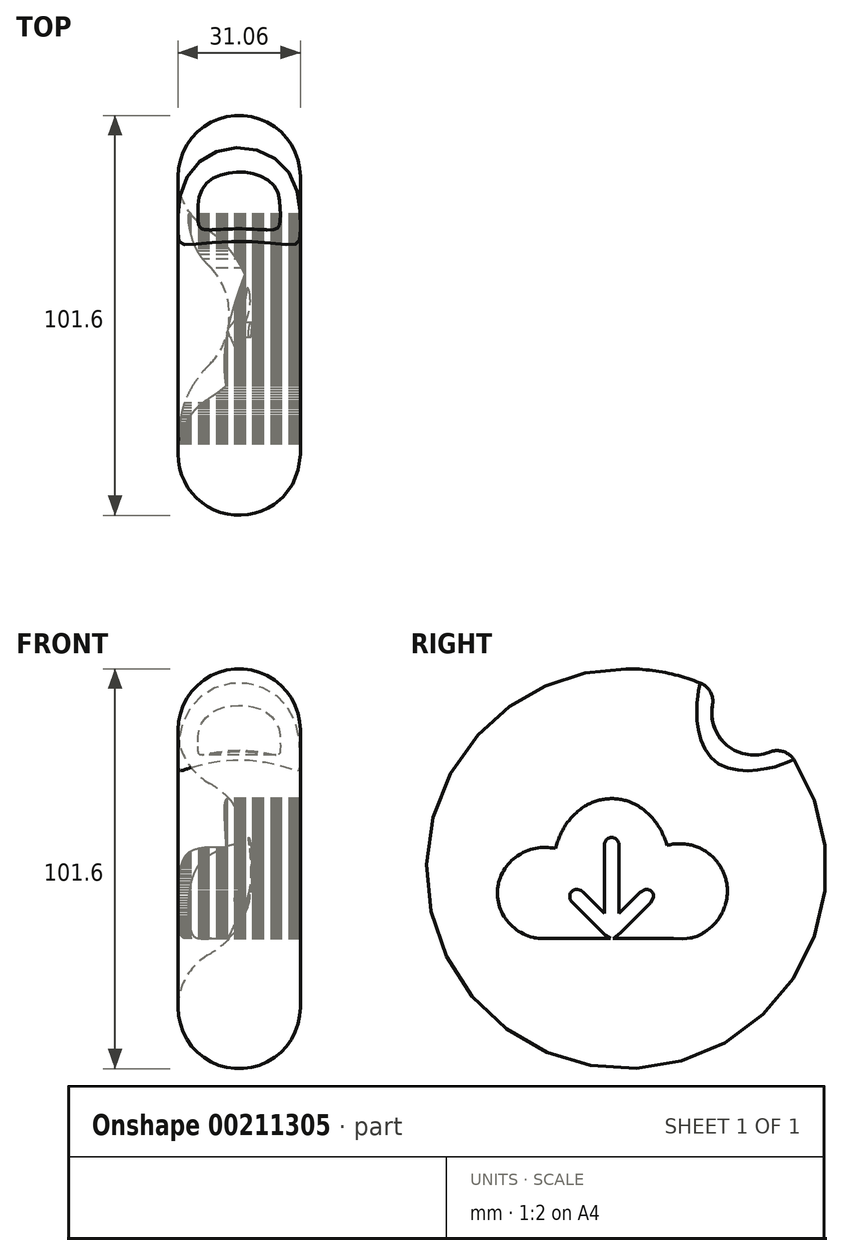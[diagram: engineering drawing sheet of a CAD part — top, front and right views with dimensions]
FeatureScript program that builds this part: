
annotation { "Feature Type Name" : "Feature", "Feature Type Description" : "" }
export const myFeature = defineFeature(function(context is Context, id is Id, definition is map)
    precondition{}
    {
        {
            var Q0;
            Q0=qCreatedBy(makeId("Top.planeOp"),FACE);
            var sketch = newSketch(context, id + "F0", { "sketchPlane" : qUnion([Q0])});
            skArc(sketch, "E0", {"start": v(10.16, -18.2) * mm, "mid": v(18.8, -9) * mm, "end": v(20.56, 3.5) * mm});
            skArc(sketch, "E1", {"start": v(10.16, -18.2) * mm, "mid": v(9.87, -45.16) * mm, "end": v(33.26, -31.77) * mm});
            skLineSegment(sketch, "E2", {"start": v(33.26, -4.3) * mm, "end": v(33.26, 3.5) * mm});
            skLineSegment(sketch, "E3", {"start": v(33.26, -4.3) * mm, "end": v(33.26, -31.77) * mm});
            skLineSegment(sketch, "E4", {"start": v(20.56, 3.5) * mm, "end": v(46.67, 3.5) * mm});
            skPoint(sketch, "E5.orphan", {"position": v(33.26, 20.85) * mm});
            skSolve(sketch);
        }
        {
            var Q0;
            {var subQ1=sQuery(id+"F0.wireOp",EDGE,"E0");Q0=makeQuery(id+"F0.imprint","IMPRINT",FACE,{"disambiguationData":[TD([[makeQuery(id+"F0.imprint","IMPRINT",EDGE,{"derivedFrom":subQ1}),-1.0]])]});}
            var Q1;
            Q1=sQuery(id+"F0.wireOp",EDGE,"E4");
            revolve(context, id + "F1", {"entities" : qUnion([Q0]), "axis" : qUnion([Q1]), "revolveType" : RevolveType.FULL});
        }
        {
            var Q0;
            Q0=qCreatedBy(makeId("Right.planeOp"),FACE);
            var sketch = newSketch(context, id + "F2", { "sketchPlane" : qUnion([Q0])});
            skCircle(sketch, "E6", {"center": v(35.9, 39.54) * mm, "radius": 10.68 * mm});
            skSolve(sketch);
        }
        {
            var Q0;
            Q0=makeQuery(id+"F2.imprint","IMPRINT",FACE,{"disambiguationData":[TD([[makeQuery(id+"F2.imprint","IMPRINT",EDGE,{"derivedFrom":sQuery(id+"F2.wireOp",EDGE,"E6")}),1.0]])]});
            extrude(context, id + "F3", {"entities" : qUnion([Q0]), "operationType" : NewBodyOperationType.REMOVE, "depth" : 53.85 * mm});
        }
        {
            var Q0;
            Q0=makeQuery(id+"F3.boolean.opBoolean","INTERSECT",EDGE,{"derivedFrom":[makeQuery(id+"F1.opRevolve","SWEPT_FACE",FACE,{"disambiguationData":[OSD([sQuery(id+"F0.wireOp",EDGE,"E1")])]}),makeQuery(id+"F3.opExtrude","SWEPT_FACE",FACE,{"disambiguationData":[OSD([sQuery(id+"F2.wireOp",EDGE,"E6")])]})]});
            fillet(context, id + "F4", {"entities" : qUnion([Q0]), "radius" : 5.08 * mm, "tangentPropagation" : true, "allowEdgeOverflow" : false});
        }
        {
            var Q0;
            Q0=qCreatedBy(makeId("Right.planeOp"),FACE);
            var sketch = newSketch(context, id + "F5", { "sketchPlane" : qUnion([Q0])});
            skLineSegment(sketch, "E7", {"start": v(-6.98, 15.9) * mm, "end": v(-6.63, 16.1) * mm});
            skLineSegment(sketch, "E8", {"start": v(-6.63, 16.1) * mm, "end": v(-6.28, 16.3) * mm});
            skLineSegment(sketch, "E9", {"start": v(-6.28, 16.3) * mm, "end": v(-5.92, 16.48) * mm});
            skLineSegment(sketch, "E10", {"start": v(-5.92, 16.48) * mm, "end": v(-5.56, 16.65) * mm});
            skLineSegment(sketch, "E11", {"start": v(-5.56, 16.65) * mm, "end": v(-5.2, 16.8) * mm});
            skLineSegment(sketch, "E12", {"start": v(-5.2, 16.8) * mm, "end": v(-4.82, 16.95) * mm});
            skLineSegment(sketch, "E13", {"start": v(-4.82, 16.95) * mm, "end": v(-4.45, 17.09) * mm});
            skLineSegment(sketch, "E14", {"start": v(-4.45, 17.09) * mm, "end": v(-4.07, 17.21) * mm});
            skLineSegment(sketch, "E15", {"start": v(-4.07, 17.21) * mm, "end": v(-3.68, 17.32) * mm});
            skLineSegment(sketch, "E16", {"start": v(-3.68, 17.32) * mm, "end": v(-3.3, 17.43) * mm});
            skLineSegment(sketch, "E17", {"start": v(-3.3, 17.43) * mm, "end": v(-2.9, 17.51) * mm});
            skLineSegment(sketch, "E18", {"start": v(-2.9, 17.51) * mm, "end": v(-2.51, 17.6) * mm});
            skLineSegment(sketch, "E19", {"start": v(-2.51, 17.6) * mm, "end": v(-2.12, 17.66) * mm});
            skLineSegment(sketch, "E20", {"start": v(-2.12, 17.66) * mm, "end": v(-1.72, 17.71) * mm});
            skLineSegment(sketch, "E21", {"start": v(-1.72, 17.71) * mm, "end": v(-1.32, 17.75) * mm});
            skLineSegment(sketch, "E22", {"start": v(-1.32, 17.75) * mm, "end": v(-0.92, 17.78) * mm});
            skLineSegment(sketch, "E23", {"start": v(-0.92, 17.78) * mm, "end": v(-0.52, 17.8) * mm});
            skLineSegment(sketch, "E24", {"start": v(-0.52, 17.8) * mm, "end": v(-0.12, 17.8) * mm});
            skLineSegment(sketch, "E25", {"start": v(-0.12, 17.8) * mm, "end": v(0.28, 17.8) * mm});
            skLineSegment(sketch, "E26", {"start": v(0.28, 17.8) * mm, "end": v(0.68, 17.78) * mm});
            skLineSegment(sketch, "E27", {"start": v(0.68, 17.78) * mm, "end": v(1.08, 17.75) * mm});
            skLineSegment(sketch, "E28", {"start": v(1.08, 17.75) * mm, "end": v(1.47, 17.7) * mm});
            skLineSegment(sketch, "E29", {"start": v(1.47, 17.7) * mm, "end": v(1.87, 17.65) * mm});
            skLineSegment(sketch, "E30", {"start": v(1.87, 17.65) * mm, "end": v(2.26, 17.58) * mm});
            skLineSegment(sketch, "E31", {"start": v(2.26, 17.58) * mm, "end": v(2.66, 17.5) * mm});
            skLineSegment(sketch, "E32", {"start": v(2.66, 17.5) * mm, "end": v(3.05, 17.4) * mm});
            skLineSegment(sketch, "E33", {"start": v(3.05, 17.4) * mm, "end": v(3.43, 17.3) * mm});
            skLineSegment(sketch, "E34", {"start": v(3.43, 17.3) * mm, "end": v(3.82, 17.18) * mm});
            skLineSegment(sketch, "E35", {"start": v(3.82, 17.18) * mm, "end": v(4.2, 17.05) * mm});
            skLineSegment(sketch, "E36", {"start": v(4.2, 17.05) * mm, "end": v(4.7, 16.86) * mm});
            skLineSegment(sketch, "E37", {"start": v(4.7, 16.86) * mm, "end": v(5.18, 16.65) * mm});
            skLineSegment(sketch, "E38", {"start": v(5.18, 16.65) * mm, "end": v(5.66, 16.42) * mm});
            skLineSegment(sketch, "E39", {"start": v(5.66, 16.42) * mm, "end": v(6.13, 16.17) * mm});
            skLineSegment(sketch, "E40", {"start": v(6.13, 16.17) * mm, "end": v(6.58, 15.91) * mm});
            skLineSegment(sketch, "E41", {"start": v(6.58, 15.91) * mm, "end": v(7.03, 15.63) * mm});
            skLineSegment(sketch, "E42", {"start": v(7.03, 15.63) * mm, "end": v(7.46, 15.34) * mm});
            skLineSegment(sketch, "E43", {"start": v(7.46, 15.34) * mm, "end": v(7.88, 15.02) * mm});
            skLineSegment(sketch, "E44", {"start": v(7.88, 15.02) * mm, "end": v(8.3, 14.7) * mm});
            skLineSegment(sketch, "E45", {"start": v(8.3, 14.7) * mm, "end": v(8.7, 14.36) * mm});
            skLineSegment(sketch, "E46", {"start": v(8.7, 14.36) * mm, "end": v(9.08, 14) * mm});
            skLineSegment(sketch, "E47", {"start": v(9.08, 14) * mm, "end": v(9.46, 13.63) * mm});
            skLineSegment(sketch, "E48", {"start": v(9.46, 13.63) * mm, "end": v(9.82, 13.25) * mm});
            skLineSegment(sketch, "E49", {"start": v(9.82, 13.25) * mm, "end": v(10.17, 12.86) * mm});
            skLineSegment(sketch, "E50", {"start": v(10.17, 12.86) * mm, "end": v(10.51, 12.45) * mm});
            skLineSegment(sketch, "E51", {"start": v(10.51, 12.45) * mm, "end": v(10.84, 12.04) * mm});
            skLineSegment(sketch, "E52", {"start": v(10.84, 12.04) * mm, "end": v(11.15, 11.61) * mm});
            skLineSegment(sketch, "E53", {"start": v(11.15, 11.61) * mm, "end": v(11.46, 11.18) * mm});
            skLineSegment(sketch, "E54", {"start": v(11.46, 11.18) * mm, "end": v(11.74, 10.73) * mm});
            skLineSegment(sketch, "E55", {"start": v(11.74, 10.73) * mm, "end": v(12.02, 10.28) * mm});
            skLineSegment(sketch, "E56", {"start": v(12.02, 10.28) * mm, "end": v(12.28, 9.82) * mm});
            skLineSegment(sketch, "E57", {"start": v(12.28, 9.82) * mm, "end": v(12.53, 9.35) * mm});
            skLineSegment(sketch, "E58", {"start": v(12.53, 9.35) * mm, "end": v(12.76, 8.88) * mm});
            skLineSegment(sketch, "E59", {"start": v(12.76, 8.88) * mm, "end": v(12.98, 8.4) * mm});
            skLineSegment(sketch, "E60", {"start": v(12.98, 8.4) * mm, "end": v(13.19, 7.9) * mm});
            skLineSegment(sketch, "E61", {"start": v(13.19, 7.9) * mm, "end": v(13.38, 7.42) * mm});
            skLineSegment(sketch, "E62", {"start": v(13.38, 7.42) * mm, "end": v(13.56, 6.92) * mm});
            skLineSegment(sketch, "E63", {"start": v(13.56, 6.92) * mm, "end": v(13.72, 6.42) * mm});
            skLineSegment(sketch, "E64", {"start": v(13.72, 6.42) * mm, "end": v(13.87, 5.92) * mm});
            skLineSegment(sketch, "E65", {"start": v(13.87, 5.92) * mm, "end": v(14.25, 6.02) * mm});
            skLineSegment(sketch, "E66", {"start": v(14.25, 6.02) * mm, "end": v(14.63, 6.1) * mm});
            skLineSegment(sketch, "E67", {"start": v(14.63, 6.1) * mm, "end": v(15, 6.18) * mm});
            skLineSegment(sketch, "E68", {"start": v(15, 6.18) * mm, "end": v(15.4, 6.24) * mm});
            skLineSegment(sketch, "E69", {"start": v(15.4, 6.24) * mm, "end": v(15.78, 6.3) * mm});
            skLineSegment(sketch, "E70", {"start": v(15.78, 6.3) * mm, "end": v(16.17, 6.33) * mm});
            skLineSegment(sketch, "E71", {"start": v(16.17, 6.33) * mm, "end": v(16.56, 6.35) * mm});
            skLineSegment(sketch, "E72", {"start": v(16.56, 6.35) * mm, "end": v(16.94, 6.36) * mm});
            skLineSegment(sketch, "E73", {"start": v(16.94, 6.36) * mm, "end": v(17.33, 6.36) * mm});
            skLineSegment(sketch, "E74", {"start": v(17.33, 6.36) * mm, "end": v(17.72, 6.35) * mm});
            skLineSegment(sketch, "E75", {"start": v(17.72, 6.35) * mm, "end": v(18.11, 6.32) * mm});
            skLineSegment(sketch, "E76", {"start": v(18.11, 6.32) * mm, "end": v(18.5, 6.28) * mm});
            skLineSegment(sketch, "E77", {"start": v(18.5, 6.28) * mm, "end": v(18.88, 6.23) * mm});
            skLineSegment(sketch, "E78", {"start": v(18.88, 6.23) * mm, "end": v(19.27, 6.17) * mm});
            skLineSegment(sketch, "E79", {"start": v(19.27, 6.17) * mm, "end": v(19.65, 6.1) * mm});
            skLineSegment(sketch, "E80", {"start": v(19.65, 6.1) * mm, "end": v(20.03, 6.01) * mm});
            skLineSegment(sketch, "E81", {"start": v(20.03, 6.01) * mm, "end": v(20.4, 5.91) * mm});
            skLineSegment(sketch, "E82", {"start": v(20.4, 5.91) * mm, "end": v(20.78, 5.8) * mm});
            skLineSegment(sketch, "E83", {"start": v(20.78, 5.8) * mm, "end": v(21.15, 5.68) * mm});
            skLineSegment(sketch, "E84", {"start": v(21.15, 5.68) * mm, "end": v(21.51, 5.55) * mm});
            skLineSegment(sketch, "E85", {"start": v(21.51, 5.55) * mm, "end": v(21.87, 5.4) * mm});
            skLineSegment(sketch, "E86", {"start": v(21.87, 5.4) * mm, "end": v(22.23, 5.24) * mm});
            skLineSegment(sketch, "E87", {"start": v(22.23, 5.24) * mm, "end": v(22.58, 5.07) * mm});
            skLineSegment(sketch, "E88", {"start": v(22.58, 5.07) * mm, "end": v(22.92, 4.9) * mm});
            skLineSegment(sketch, "E89", {"start": v(22.92, 4.9) * mm, "end": v(23.26, 4.7) * mm});
            skLineSegment(sketch, "E90", {"start": v(23.26, 4.7) * mm, "end": v(23.59, 4.5) * mm});
            skLineSegment(sketch, "E91", {"start": v(23.59, 4.5) * mm, "end": v(23.91, 4.28) * mm});
            skLineSegment(sketch, "E92", {"start": v(23.91, 4.28) * mm, "end": v(24.23, 4.05) * mm});
            skLineSegment(sketch, "E93", {"start": v(24.23, 4.05) * mm, "end": v(24.54, 3.81) * mm});
            skLineSegment(sketch, "E94", {"start": v(24.54, 3.81) * mm, "end": v(24.82, 3.59) * mm});
            skLineSegment(sketch, "E95", {"start": v(24.82, 3.59) * mm, "end": v(25.1, 3.36) * mm});
            skLineSegment(sketch, "E96", {"start": v(25.1, 3.36) * mm, "end": v(25.36, 3.12) * mm});
            skLineSegment(sketch, "E97", {"start": v(25.36, 3.12) * mm, "end": v(25.62, 2.87) * mm});
            skLineSegment(sketch, "E98", {"start": v(25.62, 2.87) * mm, "end": v(25.87, 2.61) * mm});
            skLineSegment(sketch, "E99", {"start": v(25.87, 2.61) * mm, "end": v(26.11, 2.35) * mm});
            skLineSegment(sketch, "E100", {"start": v(26.11, 2.35) * mm, "end": v(26.35, 2.08) * mm});
            skLineSegment(sketch, "E101", {"start": v(26.35, 2.08) * mm, "end": v(26.57, 1.8) * mm});
            skLineSegment(sketch, "E102", {"start": v(26.57, 1.8) * mm, "end": v(26.8, 1.52) * mm});
            skLineSegment(sketch, "E103", {"start": v(26.8, 1.52) * mm, "end": v(27, 1.23) * mm});
            skLineSegment(sketch, "E104", {"start": v(27, 1.23) * mm, "end": v(27.2, 0.93) * mm});
            skLineSegment(sketch, "E105", {"start": v(27.2, 0.93) * mm, "end": v(27.4, 0.63) * mm});
            skLineSegment(sketch, "E106", {"start": v(27.4, 0.63) * mm, "end": v(27.58, 0.32) * mm});
            skLineSegment(sketch, "E107", {"start": v(27.58, 0.32) * mm, "end": v(27.75, 0.01) * mm});
            skLineSegment(sketch, "E108", {"start": v(27.75, 0.01) * mm, "end": v(27.92, -0.3) * mm});
            skLineSegment(sketch, "E109", {"start": v(27.92, -0.3) * mm, "end": v(28.08, -0.63) * mm});
            skLineSegment(sketch, "E110", {"start": v(28.08, -0.63) * mm, "end": v(28.22, -0.95) * mm});
            skLineSegment(sketch, "E111", {"start": v(28.22, -0.95) * mm, "end": v(28.36, -1.28) * mm});
            skLineSegment(sketch, "E112", {"start": v(28.36, -1.28) * mm, "end": v(28.49, -1.62) * mm});
            skLineSegment(sketch, "E113", {"start": v(28.49, -1.62) * mm, "end": v(28.6, -1.95) * mm});
            skLineSegment(sketch, "E114", {"start": v(28.6, -1.95) * mm, "end": v(28.71, -2.3) * mm});
            skLineSegment(sketch, "E115", {"start": v(28.71, -2.3) * mm, "end": v(28.81, -2.64) * mm});
            skLineSegment(sketch, "E116", {"start": v(28.81, -2.64) * mm, "end": v(28.9, -2.99) * mm});
            skLineSegment(sketch, "E117", {"start": v(28.9, -2.99) * mm, "end": v(28.98, -3.34) * mm});
            skLineSegment(sketch, "E118", {"start": v(28.98, -3.34) * mm, "end": v(29.04, -3.69) * mm});
            skLineSegment(sketch, "E119", {"start": v(29.04, -3.69) * mm, "end": v(29.1, -4.04) * mm});
            skLineSegment(sketch, "E120", {"start": v(29.1, -4.04) * mm, "end": v(29.14, -4.4) * mm});
            skLineSegment(sketch, "E121", {"start": v(29.14, -4.4) * mm, "end": v(29.18, -4.76) * mm});
            skLineSegment(sketch, "E122", {"start": v(29.18, -4.76) * mm, "end": v(29.2, -5.11) * mm});
            skLineSegment(sketch, "E123", {"start": v(29.2, -5.11) * mm, "end": v(29.2, -6.08) * mm});
            skLineSegment(sketch, "E124", {"start": v(29.2, -6.08) * mm, "end": v(29.18, -6.5) * mm});
            skLineSegment(sketch, "E125", {"start": v(29.18, -6.5) * mm, "end": v(29.15, -6.9) * mm});
            skLineSegment(sketch, "E126", {"start": v(29.15, -6.9) * mm, "end": v(29.1, -7.31) * mm});
            skLineSegment(sketch, "E127", {"start": v(29.1, -7.31) * mm, "end": v(29.05, -7.72) * mm});
            skLineSegment(sketch, "E128", {"start": v(29.05, -7.72) * mm, "end": v(28.97, -8.12) * mm});
            skLineSegment(sketch, "E129", {"start": v(28.97, -8.12) * mm, "end": v(28.88, -8.52) * mm});
            skLineSegment(sketch, "E130", {"start": v(28.88, -8.52) * mm, "end": v(28.78, -8.92) * mm});
            skLineSegment(sketch, "E131", {"start": v(28.78, -8.92) * mm, "end": v(28.66, -9.31) * mm});
            skLineSegment(sketch, "E132", {"start": v(28.66, -9.31) * mm, "end": v(28.53, -9.7) * mm});
            skLineSegment(sketch, "E133", {"start": v(28.53, -9.7) * mm, "end": v(28.39, -10.08) * mm});
            skLineSegment(sketch, "E134", {"start": v(28.39, -10.08) * mm, "end": v(28.23, -10.46) * mm});
            skLineSegment(sketch, "E135", {"start": v(28.23, -10.46) * mm, "end": v(28.06, -10.83) * mm});
            skLineSegment(sketch, "E136", {"start": v(28.06, -10.83) * mm, "end": v(27.88, -11.2) * mm});
            skLineSegment(sketch, "E137", {"start": v(27.88, -11.2) * mm, "end": v(27.69, -11.56) * mm});
            skLineSegment(sketch, "E138", {"start": v(27.69, -11.56) * mm, "end": v(27.48, -11.92) * mm});
            skLineSegment(sketch, "E139", {"start": v(27.48, -11.92) * mm, "end": v(27.27, -12.27) * mm});
            skLineSegment(sketch, "E140", {"start": v(27.27, -12.27) * mm, "end": v(27.04, -12.6) * mm});
            skLineSegment(sketch, "E141", {"start": v(27.04, -12.6) * mm, "end": v(26.8, -12.94) * mm});
            skLineSegment(sketch, "E142", {"start": v(26.8, -12.94) * mm, "end": v(26.55, -13.27) * mm});
            skLineSegment(sketch, "E143", {"start": v(26.55, -13.27) * mm, "end": v(26.29, -13.58) * mm});
            skLineSegment(sketch, "E144", {"start": v(26.29, -13.58) * mm, "end": v(26.02, -13.9) * mm});
            skLineSegment(sketch, "E145", {"start": v(26.02, -13.9) * mm, "end": v(25.74, -14.2) * mm});
            skLineSegment(sketch, "E146", {"start": v(25.74, -14.2) * mm, "end": v(25.45, -14.48) * mm});
            skLineSegment(sketch, "E147", {"start": v(25.45, -14.48) * mm, "end": v(25.15, -14.76) * mm});
            skLineSegment(sketch, "E148", {"start": v(25.15, -14.76) * mm, "end": v(24.84, -15.03) * mm});
            skLineSegment(sketch, "E149", {"start": v(24.84, -15.03) * mm, "end": v(24.52, -15.3) * mm});
            skLineSegment(sketch, "E150", {"start": v(24.52, -15.3) * mm, "end": v(24.2, -15.54) * mm});
            skLineSegment(sketch, "E151", {"start": v(24.2, -15.54) * mm, "end": v(23.86, -15.78) * mm});
            skLineSegment(sketch, "E152", {"start": v(23.86, -15.78) * mm, "end": v(23.52, -16) * mm});
            skLineSegment(sketch, "E153", {"start": v(23.52, -16) * mm, "end": v(23.28, -16.19) * mm});
            skLineSegment(sketch, "E154", {"start": v(23.28, -16.19) * mm, "end": v(23.04, -16.36) * mm});
            skLineSegment(sketch, "E155", {"start": v(23.04, -16.36) * mm, "end": v(22.8, -16.52) * mm});
            skLineSegment(sketch, "E156", {"start": v(22.8, -16.52) * mm, "end": v(22.55, -16.66) * mm});
            skLineSegment(sketch, "E157", {"start": v(22.55, -16.66) * mm, "end": v(22.3, -16.8) * mm});
            skLineSegment(sketch, "E158", {"start": v(22.3, -16.8) * mm, "end": v(22.04, -16.93) * mm});
            skLineSegment(sketch, "E159", {"start": v(22.04, -16.93) * mm, "end": v(21.77, -17.04) * mm});
            skLineSegment(sketch, "E160", {"start": v(21.77, -17.04) * mm, "end": v(21.5, -17.15) * mm});
            skLineSegment(sketch, "E161", {"start": v(21.5, -17.15) * mm, "end": v(20.97, -17.34) * mm});
            skLineSegment(sketch, "E162", {"start": v(20.97, -17.34) * mm, "end": v(20.41, -17.49) * mm});
            skLineSegment(sketch, "E163", {"start": v(20.41, -17.49) * mm, "end": v(19.85, -17.6) * mm});
            skLineSegment(sketch, "E164", {"start": v(19.85, -17.6) * mm, "end": v(18.98, -17.73) * mm});
            skLineSegment(sketch, "E165", {"start": v(18.98, -17.73) * mm, "end": v(17.82, -17.8) * mm});
            skLineSegment(sketch, "E166", {"start": v(17.82, -17.8) * mm, "end": v(15.5, -17.75) * mm});
            skLineSegment(sketch, "E167", {"start": v(15.5, -17.75) * mm, "end": v(0.13, -17.75) * mm});
            skLineSegment(sketch, "E168", {"start": v(0.13, -17.75) * mm, "end": v(0.22, -17.73) * mm});
            skLineSegment(sketch, "E169", {"start": v(0.22, -17.73) * mm, "end": v(2.1, -16.25) * mm});
            skLineSegment(sketch, "E170", {"start": v(2.1, -16.25) * mm, "end": v(9.63, -8.72) * mm});
            skLineSegment(sketch, "E171", {"start": v(9.63, -8.72) * mm, "end": v(10.46, -7.33) * mm});
            skLineSegment(sketch, "E172", {"start": v(10.46, -7.33) * mm, "end": v(10.47, -7.2) * mm});
            skLineSegment(sketch, "E173", {"start": v(10.47, -7.2) * mm, "end": v(10.48, -6.97) * mm});
            skLineSegment(sketch, "E174", {"start": v(10.48, -6.97) * mm, "end": v(10.46, -6.74) * mm});
            skLineSegment(sketch, "E175", {"start": v(10.46, -6.74) * mm, "end": v(10.4, -6.52) * mm});
            skLineSegment(sketch, "E176", {"start": v(10.4, -6.52) * mm, "end": v(10.31, -6.3) * mm});
            skLineSegment(sketch, "E177", {"start": v(10.31, -6.3) * mm, "end": v(10.14, -6) * mm});
            skLineSegment(sketch, "E178", {"start": v(10.14, -6) * mm, "end": v(9.91, -5.74) * mm});
            skLineSegment(sketch, "E179", {"start": v(9.91, -5.74) * mm, "end": v(9.64, -5.52) * mm});
            skLineSegment(sketch, "E180", {"start": v(9.64, -5.52) * mm, "end": v(9.34, -5.35) * mm});
            skLineSegment(sketch, "E181", {"start": v(9.34, -5.35) * mm, "end": v(9.12, -5.27) * mm});
            skLineSegment(sketch, "E182", {"start": v(9.12, -5.27) * mm, "end": v(8.9, -5.22) * mm});
            skLineSegment(sketch, "E183", {"start": v(8.9, -5.22) * mm, "end": v(8.66, -5.2) * mm});
            skLineSegment(sketch, "E184", {"start": v(8.66, -5.2) * mm, "end": v(8.43, -5.22) * mm});
            skLineSegment(sketch, "E185", {"start": v(8.43, -5.22) * mm, "end": v(6.95, -6.06) * mm});
            skLineSegment(sketch, "E186", {"start": v(6.95, -6.06) * mm, "end": v(1.7, -11.3) * mm});
            skLineSegment(sketch, "E187", {"start": v(1.7, -11.3) * mm, "end": v(1.7, 5.93) * mm});
            skLineSegment(sketch, "E188", {"start": v(1.7, 5.93) * mm, "end": v(1.7, 6.05) * mm});
            skLineSegment(sketch, "E189", {"start": v(1.7, 6.05) * mm, "end": v(1.7, 6.29) * mm});
            skLineSegment(sketch, "E190", {"start": v(1.7, 6.29) * mm, "end": v(1.65, 6.52) * mm});
            skLineSegment(sketch, "E191", {"start": v(1.65, 6.52) * mm, "end": v(1.57, 6.74) * mm});
            skLineSegment(sketch, "E192", {"start": v(1.57, 6.74) * mm, "end": v(1.47, 6.95) * mm});
            skLineSegment(sketch, "E193", {"start": v(1.47, 6.95) * mm, "end": v(1.28, 7.24) * mm});
            skLineSegment(sketch, "E194", {"start": v(1.28, 7.24) * mm, "end": v(1.03, 7.5) * mm});
            skLineSegment(sketch, "E195", {"start": v(1.03, 7.5) * mm, "end": v(0.75, 7.7) * mm});
            skLineSegment(sketch, "E196", {"start": v(0.75, 7.7) * mm, "end": v(0.44, 7.85) * mm});
            skLineSegment(sketch, "E197", {"start": v(0.44, 7.85) * mm, "end": v(0.21, 7.91) * mm});
            skLineSegment(sketch, "E198", {"start": v(0.21, 7.91) * mm, "end": v(-0.02, 7.95) * mm});
            skLineSegment(sketch, "E199", {"start": v(-0.02, 7.95) * mm, "end": v(-0.25, 7.95) * mm});
            skLineSegment(sketch, "E200", {"start": v(-0.25, 7.95) * mm, "end": v(-0.49, 7.91) * mm});
            skLineSegment(sketch, "E201", {"start": v(-0.49, 7.91) * mm, "end": v(-0.77, 7.85) * mm});
            skLineSegment(sketch, "E202", {"start": v(-0.77, 7.85) * mm, "end": v(-1.11, 7.7) * mm});
            skLineSegment(sketch, "E203", {"start": v(-1.11, 7.7) * mm, "end": v(-1.48, 7.41) * mm});
            skLineSegment(sketch, "E204", {"start": v(-1.48, 7.41) * mm, "end": v(-1.81, 6.96) * mm});
            skLineSegment(sketch, "E205", {"start": v(-1.81, 6.96) * mm, "end": v(-2, 6.44) * mm});
            skLineSegment(sketch, "E206", {"start": v(-2, 6.44) * mm, "end": v(-2.06, 5.97) * mm});
            skLineSegment(sketch, "E207", {"start": v(-2.06, 5.97) * mm, "end": v(-2.07, -11.34) * mm});
            skLineSegment(sketch, "E208", {"start": v(-2.07, -11.34) * mm, "end": v(-7.4, -6) * mm});
            skLineSegment(sketch, "E209", {"start": v(-7.4, -6) * mm, "end": v(-7.99, -5.5) * mm});
            skLineSegment(sketch, "E210", {"start": v(-7.99, -5.5) * mm, "end": v(-8.85, -5.2) * mm});
            skLineSegment(sketch, "E211", {"start": v(-8.85, -5.2) * mm, "end": v(-9.4, -5.25) * mm});
            skLineSegment(sketch, "E212", {"start": v(-9.4, -5.25) * mm, "end": v(-9.53, -5.28) * mm});
            skLineSegment(sketch, "E213", {"start": v(-9.53, -5.28) * mm, "end": v(-9.66, -5.32) * mm});
            skLineSegment(sketch, "E214", {"start": v(-9.66, -5.32) * mm, "end": v(-9.79, -5.38) * mm});
            skLineSegment(sketch, "E215", {"start": v(-9.79, -5.38) * mm, "end": v(-9.9, -5.44) * mm});
            skLineSegment(sketch, "E216", {"start": v(-9.9, -5.44) * mm, "end": v(-10.02, -5.5) * mm});
            skLineSegment(sketch, "E217", {"start": v(-10.02, -5.5) * mm, "end": v(-10.12, -5.58) * mm});
            skLineSegment(sketch, "E218", {"start": v(-10.12, -5.58) * mm, "end": v(-10.32, -5.76) * mm});
            skLineSegment(sketch, "E219", {"start": v(-10.32, -5.76) * mm, "end": v(-10.48, -5.97) * mm});
            skLineSegment(sketch, "E220", {"start": v(-10.48, -5.97) * mm, "end": v(-10.62, -6.2) * mm});
            skLineSegment(sketch, "E221", {"start": v(-10.62, -6.2) * mm, "end": v(-10.72, -6.44) * mm});
            skLineSegment(sketch, "E222", {"start": v(-10.72, -6.44) * mm, "end": v(-10.8, -6.7) * mm});
            skLineSegment(sketch, "E223", {"start": v(-10.8, -6.7) * mm, "end": v(-10.83, -6.96) * mm});
            skLineSegment(sketch, "E224", {"start": v(-10.83, -6.96) * mm, "end": v(-10.84, -7.22) * mm});
            skLineSegment(sketch, "E225", {"start": v(-10.84, -7.22) * mm, "end": v(-10.8, -7.49) * mm});
            skLineSegment(sketch, "E226", {"start": v(-10.8, -7.49) * mm, "end": v(-10.73, -7.74) * mm});
            skLineSegment(sketch, "E227", {"start": v(-10.73, -7.74) * mm, "end": v(-10.68, -7.86) * mm});
            skLineSegment(sketch, "E228", {"start": v(-10.68, -7.86) * mm, "end": v(-10.62, -7.98) * mm});
            skLineSegment(sketch, "E229", {"start": v(-10.62, -7.98) * mm, "end": v(-10.55, -8.1) * mm});
            skLineSegment(sketch, "E230", {"start": v(-10.55, -8.1) * mm, "end": v(-10.47, -8.2) * mm});
            skLineSegment(sketch, "E231", {"start": v(-10.47, -8.2) * mm, "end": v(-10.37, -8.3) * mm});
            skLineSegment(sketch, "E232", {"start": v(-10.37, -8.3) * mm, "end": v(-1.71, -17) * mm});
            skLineSegment(sketch, "E233", {"start": v(-1.71, -17) * mm, "end": v(-0.45, -17.76) * mm});
            skLineSegment(sketch, "E234", {"start": v(-0.45, -17.76) * mm, "end": v(-14.6, -17.74) * mm});
            skLineSegment(sketch, "E235", {"start": v(-14.6, -17.74) * mm, "end": v(-18.77, -17.72) * mm});
            skLineSegment(sketch, "E236", {"start": v(-18.77, -17.72) * mm, "end": v(-19.44, -17.61) * mm});
            skLineSegment(sketch, "E237", {"start": v(-19.44, -17.61) * mm, "end": v(-20.1, -17.47) * mm});
            skLineSegment(sketch, "E238", {"start": v(-20.1, -17.47) * mm, "end": v(-20.75, -17.3) * mm});
            skLineSegment(sketch, "E239", {"start": v(-20.75, -17.3) * mm, "end": v(-21.4, -17.07) * mm});
            skLineSegment(sketch, "E240", {"start": v(-21.4, -17.07) * mm, "end": v(-22.03, -16.82) * mm});
            skLineSegment(sketch, "E241", {"start": v(-22.03, -16.82) * mm, "end": v(-22.64, -16.54) * mm});
            skLineSegment(sketch, "E242", {"start": v(-22.64, -16.54) * mm, "end": v(-23.24, -16.22) * mm});
            skLineSegment(sketch, "E243", {"start": v(-23.24, -16.22) * mm, "end": v(-23.82, -15.87) * mm});
            skLineSegment(sketch, "E244", {"start": v(-23.82, -15.87) * mm, "end": v(-24.38, -15.49) * mm});
            skLineSegment(sketch, "E245", {"start": v(-24.38, -15.49) * mm, "end": v(-24.92, -15.08) * mm});
            skLineSegment(sketch, "E246", {"start": v(-24.92, -15.08) * mm, "end": v(-25.43, -14.64) * mm});
            skLineSegment(sketch, "E247", {"start": v(-25.43, -14.64) * mm, "end": v(-25.92, -14.16) * mm});
            skLineSegment(sketch, "E248", {"start": v(-25.92, -14.16) * mm, "end": v(-26.38, -13.67) * mm});
            skLineSegment(sketch, "E249", {"start": v(-26.38, -13.67) * mm, "end": v(-26.81, -13.14) * mm});
            skLineSegment(sketch, "E250", {"start": v(-26.81, -13.14) * mm, "end": v(-27.01, -12.87) * mm});
            skLineSegment(sketch, "E251", {"start": v(-27.01, -12.87) * mm, "end": v(-27.2, -12.6) * mm});
            skLineSegment(sketch, "E252", {"start": v(-27.2, -12.6) * mm, "end": v(-27.57, -12.05) * mm});
            skLineSegment(sketch, "E253", {"start": v(-27.57, -12.05) * mm, "end": v(-27.9, -11.48) * mm});
            skLineSegment(sketch, "E254", {"start": v(-27.9, -11.48) * mm, "end": v(-28.18, -10.9) * mm});
            skLineSegment(sketch, "E255", {"start": v(-28.18, -10.9) * mm, "end": v(-28.44, -10.29) * mm});
            skLineSegment(sketch, "E256", {"start": v(-28.44, -10.29) * mm, "end": v(-28.65, -9.67) * mm});
            skLineSegment(sketch, "E257", {"start": v(-28.65, -9.67) * mm, "end": v(-28.84, -9.04) * mm});
            skLineSegment(sketch, "E258", {"start": v(-28.84, -9.04) * mm, "end": v(-28.98, -8.4) * mm});
            skLineSegment(sketch, "E259", {"start": v(-28.98, -8.4) * mm, "end": v(-29.1, -7.76) * mm});
            skLineSegment(sketch, "E260", {"start": v(-29.1, -7.76) * mm, "end": v(-29.17, -7.1) * mm});
            skLineSegment(sketch, "E261", {"start": v(-29.17, -7.1) * mm, "end": v(-29.2, -6.45) * mm});
            skLineSegment(sketch, "E262", {"start": v(-29.2, -6.45) * mm, "end": v(-29.2, -5.8) * mm});
            skLineSegment(sketch, "E263", {"start": v(-29.2, -5.8) * mm, "end": v(-29.16, -5.14) * mm});
            skLineSegment(sketch, "E264", {"start": v(-29.16, -5.14) * mm, "end": v(-29.07, -4.5) * mm});
            skLineSegment(sketch, "E265", {"start": v(-29.07, -4.5) * mm, "end": v(-28.96, -3.85) * mm});
            skLineSegment(sketch, "E266", {"start": v(-28.96, -3.85) * mm, "end": v(-28.88, -3.52) * mm});
            skLineSegment(sketch, "E267", {"start": v(-28.88, -3.52) * mm, "end": v(-28.7, -2.89) * mm});
            skLineSegment(sketch, "E268", {"start": v(-28.7, -2.89) * mm, "end": v(-28.5, -2.27) * mm});
            skLineSegment(sketch, "E269", {"start": v(-28.5, -2.27) * mm, "end": v(-28.25, -1.66) * mm});
            skLineSegment(sketch, "E270", {"start": v(-28.25, -1.66) * mm, "end": v(-27.96, -1.07) * mm});
            skLineSegment(sketch, "E271", {"start": v(-27.96, -1.07) * mm, "end": v(-27.64, -0.5) * mm});
            skLineSegment(sketch, "E272", {"start": v(-27.64, -0.5) * mm, "end": v(-27.3, 0.06) * mm});
            skLineSegment(sketch, "E273", {"start": v(-27.3, 0.06) * mm, "end": v(-26.91, 0.6) * mm});
            skLineSegment(sketch, "E274", {"start": v(-26.91, 0.6) * mm, "end": v(-26.5, 1.11) * mm});
            skLineSegment(sketch, "E275", {"start": v(-26.5, 1.11) * mm, "end": v(-26.07, 1.6) * mm});
            skLineSegment(sketch, "E276", {"start": v(-26.07, 1.6) * mm, "end": v(-25.6, 2.07) * mm});
            skLineSegment(sketch, "E277", {"start": v(-25.6, 2.07) * mm, "end": v(-25.11, 2.51) * mm});
            skLineSegment(sketch, "E278", {"start": v(-25.11, 2.51) * mm, "end": v(-24.6, 2.92) * mm});
            skLineSegment(sketch, "E279", {"start": v(-24.6, 2.92) * mm, "end": v(-24.07, 3.3) * mm});
            skLineSegment(sketch, "E280", {"start": v(-24.07, 3.3) * mm, "end": v(-23.51, 3.66) * mm});
            skLineSegment(sketch, "E281", {"start": v(-23.51, 3.66) * mm, "end": v(-23.23, 3.82) * mm});
            skLineSegment(sketch, "E282", {"start": v(-23.23, 3.82) * mm, "end": v(-22.66, 4.13) * mm});
            skLineSegment(sketch, "E283", {"start": v(-22.66, 4.13) * mm, "end": v(-22.07, 4.4) * mm});
            skLineSegment(sketch, "E284", {"start": v(-22.07, 4.4) * mm, "end": v(-21.46, 4.65) * mm});
            skLineSegment(sketch, "E285", {"start": v(-21.46, 4.65) * mm, "end": v(-20.84, 4.85) * mm});
            skLineSegment(sketch, "E286", {"start": v(-20.84, 4.85) * mm, "end": v(-20.22, 5.03) * mm});
            skLineSegment(sketch, "E287", {"start": v(-20.22, 5.03) * mm, "end": v(-19.58, 5.18) * mm});
            skLineSegment(sketch, "E288", {"start": v(-19.58, 5.18) * mm, "end": v(-18.94, 5.29) * mm});
            skLineSegment(sketch, "E289", {"start": v(-18.94, 5.29) * mm, "end": v(-18.3, 5.37) * mm});
            skLineSegment(sketch, "E290", {"start": v(-18.3, 5.37) * mm, "end": v(-17.64, 5.41) * mm});
            skLineSegment(sketch, "E291", {"start": v(-17.64, 5.41) * mm, "end": v(-17, 5.42) * mm});
            skLineSegment(sketch, "E292", {"start": v(-17, 5.42) * mm, "end": v(-16.34, 5.4) * mm});
            skLineSegment(sketch, "E293", {"start": v(-16.34, 5.4) * mm, "end": v(-15.69, 5.35) * mm});
            skLineSegment(sketch, "E294", {"start": v(-15.69, 5.35) * mm, "end": v(-15.04, 5.26) * mm});
            skLineSegment(sketch, "E295", {"start": v(-15.04, 5.26) * mm, "end": v(-14.4, 5.14) * mm});
            skLineSegment(sketch, "E296", {"start": v(-14.4, 5.14) * mm, "end": v(-14.3, 5.59) * mm});
            skLineSegment(sketch, "E297", {"start": v(-14.3, 5.59) * mm, "end": v(-14.18, 6.03) * mm});
            skLineSegment(sketch, "E298", {"start": v(-14.18, 6.03) * mm, "end": v(-14.05, 6.48) * mm});
            skLineSegment(sketch, "E299", {"start": v(-14.05, 6.48) * mm, "end": v(-13.9, 6.92) * mm});
            skLineSegment(sketch, "E300", {"start": v(-13.9, 6.92) * mm, "end": v(-13.75, 7.35) * mm});
            skLineSegment(sketch, "E301", {"start": v(-13.75, 7.35) * mm, "end": v(-13.59, 7.79) * mm});
            skLineSegment(sketch, "E302", {"start": v(-13.59, 7.79) * mm, "end": v(-13.41, 8.22) * mm});
            skLineSegment(sketch, "E303", {"start": v(-13.41, 8.22) * mm, "end": v(-13.23, 8.64) * mm});
            skLineSegment(sketch, "E304", {"start": v(-13.23, 8.64) * mm, "end": v(-13.03, 9.06) * mm});
            skLineSegment(sketch, "E305", {"start": v(-13.03, 9.06) * mm, "end": v(-12.82, 9.47) * mm});
            skLineSegment(sketch, "E306", {"start": v(-12.82, 9.47) * mm, "end": v(-12.6, 9.88) * mm});
            skLineSegment(sketch, "E307", {"start": v(-12.6, 9.88) * mm, "end": v(-12.37, 10.28) * mm});
            skLineSegment(sketch, "E308", {"start": v(-12.37, 10.28) * mm, "end": v(-12.13, 10.68) * mm});
            skLineSegment(sketch, "E309", {"start": v(-12.13, 10.68) * mm, "end": v(-11.88, 11.07) * mm});
            skLineSegment(sketch, "E310", {"start": v(-11.88, 11.07) * mm, "end": v(-11.62, 11.45) * mm});
            skLineSegment(sketch, "E311", {"start": v(-11.62, 11.45) * mm, "end": v(-11.35, 11.83) * mm});
            skLineSegment(sketch, "E312", {"start": v(-11.35, 11.83) * mm, "end": v(-11.07, 12.2) * mm});
            skLineSegment(sketch, "E313", {"start": v(-11.07, 12.2) * mm, "end": v(-10.79, 12.56) * mm});
            skLineSegment(sketch, "E314", {"start": v(-10.79, 12.56) * mm, "end": v(-10.49, 12.9) * mm});
            skLineSegment(sketch, "E315", {"start": v(-10.49, 12.9) * mm, "end": v(-10.18, 13.25) * mm});
            skLineSegment(sketch, "E316", {"start": v(-10.18, 13.25) * mm, "end": v(-9.86, 13.59) * mm});
            skLineSegment(sketch, "E317", {"start": v(-9.86, 13.59) * mm, "end": v(-9.53, 13.91) * mm});
            skLineSegment(sketch, "E318", {"start": v(-9.53, 13.91) * mm, "end": v(-9.2, 14.23) * mm});
            skLineSegment(sketch, "E319", {"start": v(-9.2, 14.23) * mm, "end": v(-8.85, 14.53) * mm});
            skLineSegment(sketch, "E320", {"start": v(-8.85, 14.53) * mm, "end": v(-8.5, 14.83) * mm});
            skLineSegment(sketch, "E321", {"start": v(-8.5, 14.83) * mm, "end": v(-8.13, 15.11) * mm});
            skLineSegment(sketch, "E322", {"start": v(-8.13, 15.11) * mm, "end": v(-7.75, 15.38) * mm});
            skLineSegment(sketch, "E323", {"start": v(-7.75, 15.38) * mm, "end": v(-7.37, 15.65) * mm});
            skLineSegment(sketch, "E324", {"start": v(-7.37, 15.65) * mm, "end": v(-6.98, 15.9) * mm});
            skSolve(sketch);
        }
        {
            var Q0;
            Q0=makeQuery(id+"F5.imprint","IMPRINT",FACE,{"disambiguationData":[TD([[makeQuery(id+"F5.imprint","IMPRINT",EDGE,{"derivedFrom":sQuery(id+"F5.wireOp",EDGE,"E7")}),-1.0]])]});
            extrude(context, id + "F6", {"entities" : qUnion([Q0]), "operationType" : NewBodyOperationType.REMOVE, "depth" : 25.4 * mm});
        }
        {
            var Q0;
            Q0=qCreatedBy(makeId("Top.planeOp"),FACE);
            var sketch = newSketch(context, id + "F7", { "sketchPlane" : qUnion([Q0])});
            skLineSegment(sketch, "E325", {"start": v(17.78, -31.9) * mm, "end": v(17.78, -20.14) * mm});
            skCircle(sketch, "E326", {"center": v(17.78, -26.94) * mm, "radius": 7.62 * mm});
            skSolve(sketch);
        }
        {
            var Q0;
            Q0 = qSketchRegion(id + "F7", true);
            var Q1;
            Q1=sQuery(id+"F0.wireOp",EDGE,"E4");
            revolve(context, id + "F8", {"operationType" : NewBodyOperationType.ADD, "entities" : qUnion([Q0]), "axis" : qUnion([Q1]), "revolveType" : RevolveType.FULL});
        }
        {
            var Q0;
            Q0 = qSketchRegion(id + "F5", true);
            extrude(context, id + "F9", {"entities" : qUnion([Q0]), "operationType" : NewBodyOperationType.REMOVE, "depth" : 50.8 * mm});
        }
    });
